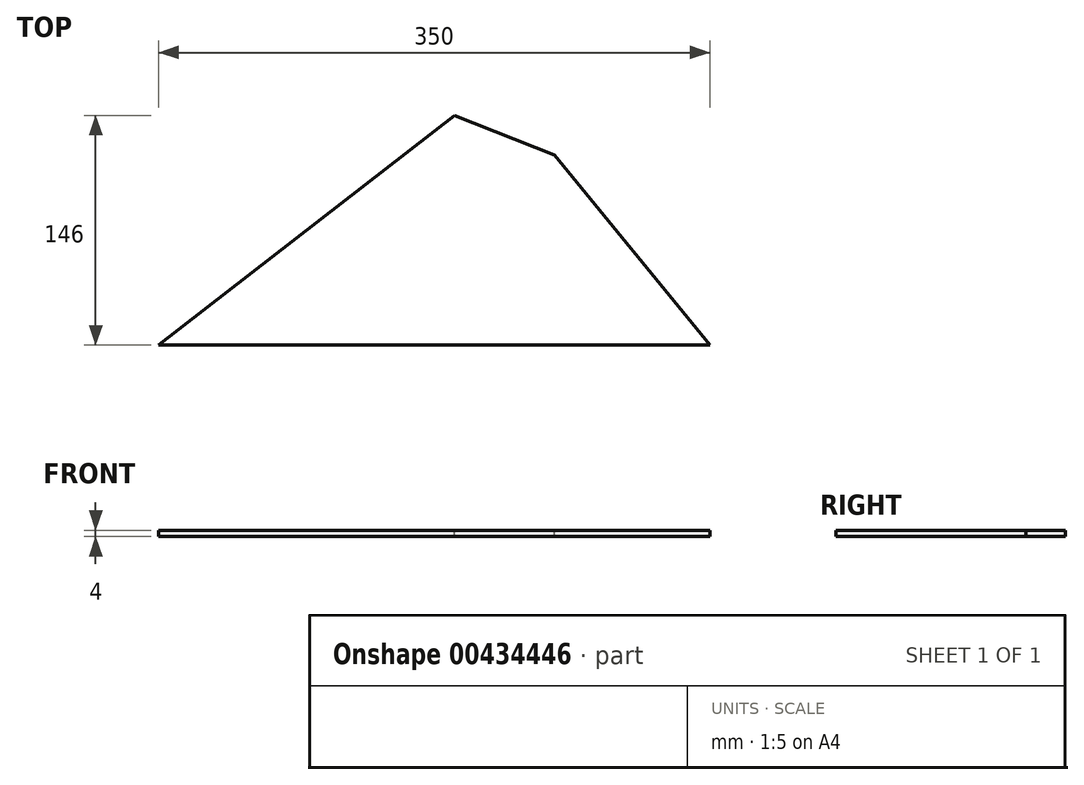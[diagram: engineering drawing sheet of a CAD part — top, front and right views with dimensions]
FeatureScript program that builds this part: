
annotation { "Feature Type Name" : "Feature", "Feature Type Description" : "" }
export const myFeature = defineFeature(function(context is Context, id is Id, definition is map)
    precondition{}
    {
        {
            var Q0;
            Q0=qCreatedBy(makeId("Right.planeOp"),FACE);
            var sketch = newSketch(context, id + "F0", { "sketchPlane" : qUnion([Q0])});
            skLineSegment(sketch, "E0.bottom", {"start": v(-146, 4) * mm, "end": v(0, 4) * mm});
            skLineSegment(sketch, "E1.top", {"start": v(-146, 0) * mm, "end": v(0, 0) * mm});
            skLineSegment(sketch, "E2.trimOffspring", {"start": v(-146, 0) * mm, "end": v(-146, 4) * mm});
            skLineSegment(sketch, "E3", {"start": v(0, 0) * mm, "end": v(0, 4) * mm});
            skSolve(sketch);
        }
        {
            var Q0;
            Q0=qSketchRegion(id+"F0",true);
            extrude(context, id + "F1", {"entities" : qUnion([Q0]), "endBound" : BoundingType.SYMMETRIC, "depth" : 350 * mm, "offsetDistance" : 25 * mm});
        }
        {
            var Q0;
            Q0=makeQuery(id+"F1.opExtrude","SWEPT_FACE",FACE,{"disambiguationData":[OSD([sQuery(id+"F0.wireOp",EDGE,"E0.bottom")])]});
            var sketch = newSketch(context, id + "F2", { "sketchPlane" : qUnion([Q0])});
            skLineSegment(sketch, "E4", {"start": v(-175, -146) * mm, "end": v(12.94, 0) * mm});
            skLineSegment(sketch, "E5", {"start": v(12.94, 0) * mm, "end": v(-175, 0) * mm});
            skLineSegment(sketch, "E6", {"start": v(-175, 0) * mm, "end": v(-175, -146) * mm});
            skLineSegment(sketch, "E7", {"start": v(175, -146) * mm, "end": v(55.94, 0) * mm});
            skLineSegment(sketch, "E8", {"start": v(55.94, 0) * mm, "end": v(175, 0) * mm});
            skLineSegment(sketch, "E9", {"start": v(175, 0) * mm, "end": v(175, -146) * mm});
            skLineSegment(sketch, "E10", {"start": v(0, -146) * mm, "end": v(0, 0) * mm, "construction": true});
            skSolve(sketch);
        }
        {
            var Q0;
            Q0=qSketchRegion(id+"F2",true);
            extrude(context, id + "F3", {"entities" : qUnion([Q0]), "operationType" : NewBodyOperationType.REMOVE, "endBound" : BoundingType.UP_TO_NEXT, "oppositeDirection" : true, "depth" : 25 * mm, "offsetDistance" : 25 * mm});
        }
        {
            var Q0;
            Q0=makeQuery(id+"F1.opExtrude","SWEPT_FACE",FACE,{"disambiguationData":[OSD([sQuery(id+"F0.wireOp",EDGE,"E0.bottom")])]});
            var sketch = newSketch(context, id + "F4", { "sketchPlane" : qUnion([Q0])});
            skLineSegment(sketch, "E11", {"start": v(12.94, 0) * mm, "end": v(76.43, -25.12) * mm});
            skLineSegment(sketch, "E12", {"start": v(76.43, -25.12) * mm, "end": v(55.94, 0) * mm});
            skLineSegment(sketch, "E13", {"start": v(55.94, 0) * mm, "end": v(12.94, 0) * mm});
            skSolve(sketch);
        }
        {
            var Q0;
            Q0 = qSketchRegion(id + "F4", true);
            extrude(context, id + "F5", {"entities" : qUnion([Q0]), "operationType" : NewBodyOperationType.REMOVE, "endBound" : BoundingType.UP_TO_NEXT, "oppositeDirection" : true, "depth" : 25 * mm, "offsetDistance" : 25 * mm});
        }
    });
